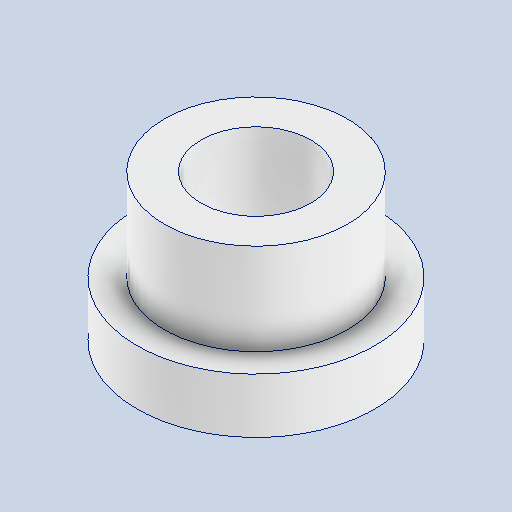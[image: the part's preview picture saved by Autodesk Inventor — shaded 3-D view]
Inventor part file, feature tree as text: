
AUTODESK INVENTOR PART (.ipt)
format: ipt  version: 2025.1 (Build 291241000, 241)  size: 123,392 bytes
history: native  units: mm
features: other x3, sketch x2
ambient origin geometry x8: Origin, YZ Plane, XZ Plane, XY Plane, X Axis, Y Axis, Z Axis, Center Point
bodies: Volumenkörper1 (feature_tree)
feature tree (5):
  other  "1173.ipt"
  other  "Volumenkörper1::1173.ipt"
  other  "TaggingFeature1"
  sketch  "Skizze1"  dims[d0=10.0mm]
  sketch  "Skizze2"
